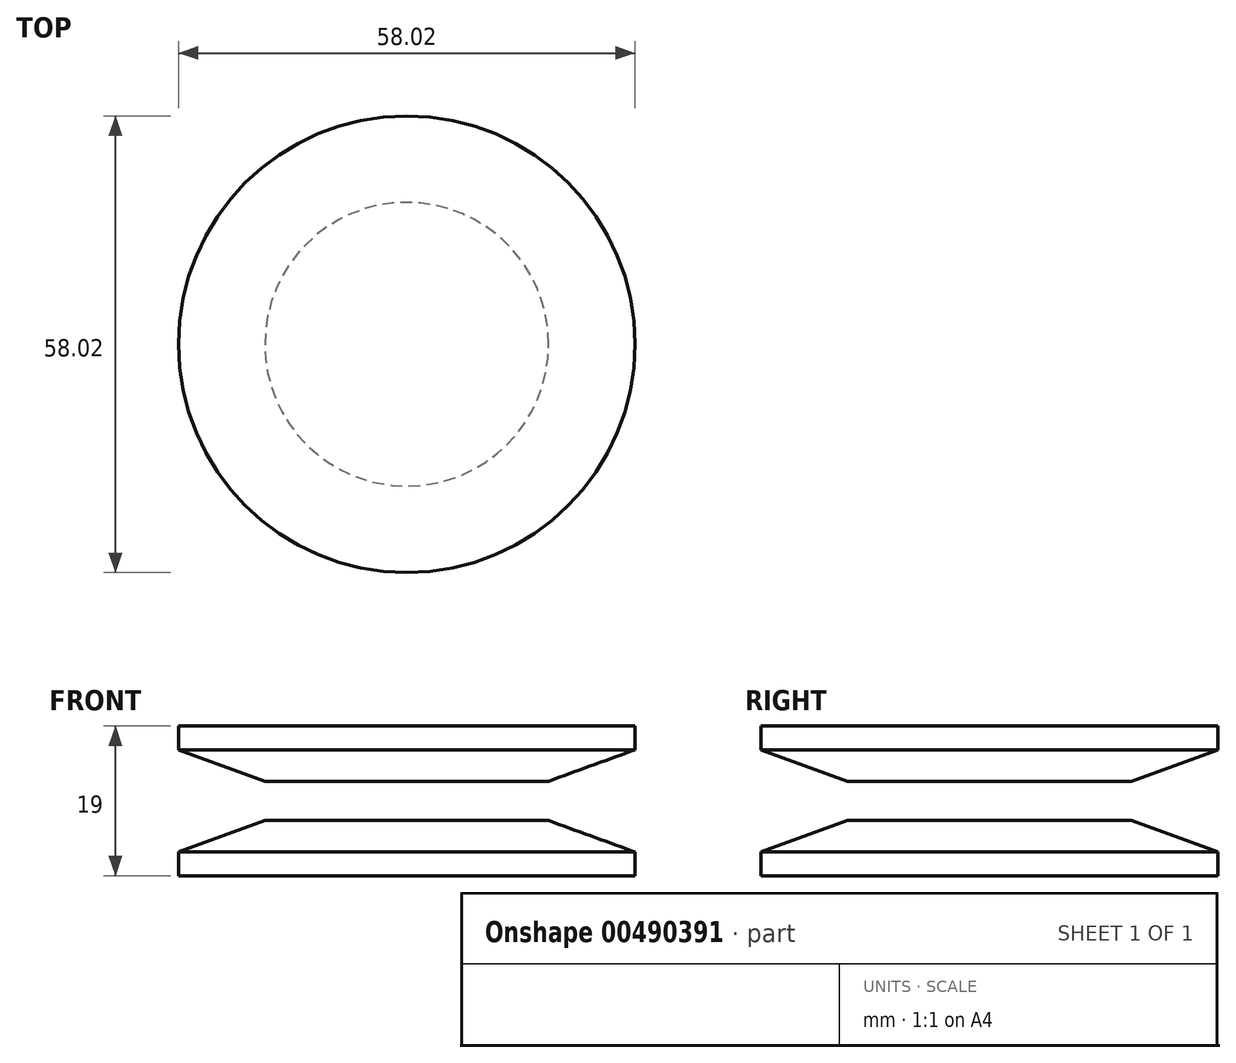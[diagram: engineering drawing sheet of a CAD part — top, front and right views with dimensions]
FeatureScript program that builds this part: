
annotation { "Feature Type Name" : "Feature", "Feature Type Description" : "" }
export const myFeature = defineFeature(function(context is Context, id is Id, definition is map)
    precondition{}
    {
        {
            var Q0;
            Q0=qCreatedBy(makeId("Front.planeOp"),FACE);
            var sketch = newSketch(context, id + "F0", { "sketchPlane" : qUnion([Q0])});
            skLineSegment(sketch, "E0", {"start": v(0, 35.64) * mm, "end": v(0, 1.23) * mm, "construction": true});
            skPoint(sketch, "E1.middle", {"position": v(0, 0) * mm});
            skLineSegment(sketch, "E2", {"start": v(0, 8.23) * mm, "end": v(29, 8.23) * mm});
            skLineSegment(sketch, "E3", {"start": v(29, 8.23) * mm, "end": v(29, 5.23) * mm});
            skLineSegment(sketch, "E4", {"start": v(29, 5.23) * mm, "end": v(18.02, 1.23) * mm});
            skLineSegment(sketch, "E5", {"start": v(18.02, -3.77) * mm, "end": v(29, -7.77) * mm});
            skLineSegment(sketch, "E6", {"start": v(29, -7.77) * mm, "end": v(29, -10.77) * mm});
            skLineSegment(sketch, "E7", {"start": v(29, -10.77) * mm, "end": v(0, -10.77) * mm});
            skLineSegment(sketch, "E8", {"start": v(0, 5.23) * mm, "end": v(29, 5.23) * mm});
            skLineSegment(sketch, "E9", {"start": v(29, -7.77) * mm, "end": v(0, -7.77) * mm});
            skLineSegment(sketch, "E10", {"start": v(18.02, 1.23) * mm, "end": v(0, 1.23) * mm});
            skLineSegment(sketch, "E11", {"start": v(0, -3.77) * mm, "end": v(18.02, -3.77) * mm});
            skLineSegment(sketch, "E12", {"start": v(0, 8.23) * mm, "end": v(0, 5.23) * mm, "construction": true});
            skLineSegment(sketch, "E13", {"start": v(0, 5.23) * mm, "end": v(0, 1.23) * mm, "construction": true});
            skLineSegment(sketch, "E14", {"start": v(0, -3.77) * mm, "end": v(0, -7.77) * mm, "construction": true});
            skLineSegment(sketch, "E15", {"start": v(0, -7.77) * mm, "end": v(0, -10.77) * mm, "construction": true});
            skLineSegment(sketch, "E16", {"start": v(0, 8.23) * mm, "end": v(0, 1.23) * mm});
            skLineSegment(sketch, "E17", {"start": v(0, 1.23) * mm, "end": v(0, 5.23) * mm});
            skLineSegment(sketch, "E18", {"start": v(0, 8.23) * mm, "end": v(0, 5.23) * mm});
            skLineSegment(sketch, "E19", {"start": v(0, -10.77) * mm, "end": v(0, -7.77) * mm});
            skLineSegment(sketch, "E20", {"start": v(0, -7.77) * mm, "end": v(0, -3.77) * mm});
            skLineSegment(sketch, "E21.trimOffspring", {"start": v(0, -3.77) * mm, "end": v(0, -34.42) * mm, "construction": true});
            skLineSegment(sketch, "E22.trimOffspring", {"start": v(0, -3.77) * mm, "end": v(0, -10.77) * mm});
            skLineSegment(sketch, "E23", {"start": v(0, 1.23) * mm, "end": v(0, -3.77) * mm});
            skLineSegment(sketch, "E24", {"start": v(18.02, -3.77) * mm, "end": v(18.02, 1.23) * mm});
            skSolve(sketch);
        }
        {
            var Q0;
            Q0=makeQuery(id+"F0.imprint","IMPRINT",FACE,{"disambiguationData":[TD([[makeQuery(id+"F0.imprint","IMPRINT",EDGE,{"derivedFrom":sQuery(id+"F0.wireOp",EDGE,"E2")}),-1.0]])]});
            var Q1;
            Q1=makeQuery(id+"F0.imprint","IMPRINT",FACE,{"disambiguationData":[TD([[makeQuery(id+"F0.imprint","IMPRINT",EDGE,{"derivedFrom":sQuery(id+"F0.wireOp",EDGE,"E6")}),-1.0]])]});
            var Q2;
            Q2=makeQuery(id+"F0.imprint","IMPRINT",FACE,{"disambiguationData":[TD([[makeQuery(id+"F0.imprint","IMPRINT",EDGE,{"derivedFrom":sQuery(id+"F0.wireOp",EDGE,"E5")}),-1.0]])]});
            var Q3;
            Q3=makeQuery(id+"F0.imprint","IMPRINT",FACE,{"disambiguationData":[TD([[makeQuery(id+"F0.imprint","IMPRINT",EDGE,{"derivedFrom":sQuery(id+"F0.wireOp",EDGE,"E8")}),-1.0]])]});
            var Q4;
            Q4=sQuery(id+"F0.wireOp",EDGE,"E0");
            revolve(context, id + "F1", {"entities" : qUnion([Q0, Q1, Q2, Q3]), "axis" : qUnion([Q4]), "revolveType" : RevolveType.FULL});
        }
    });
